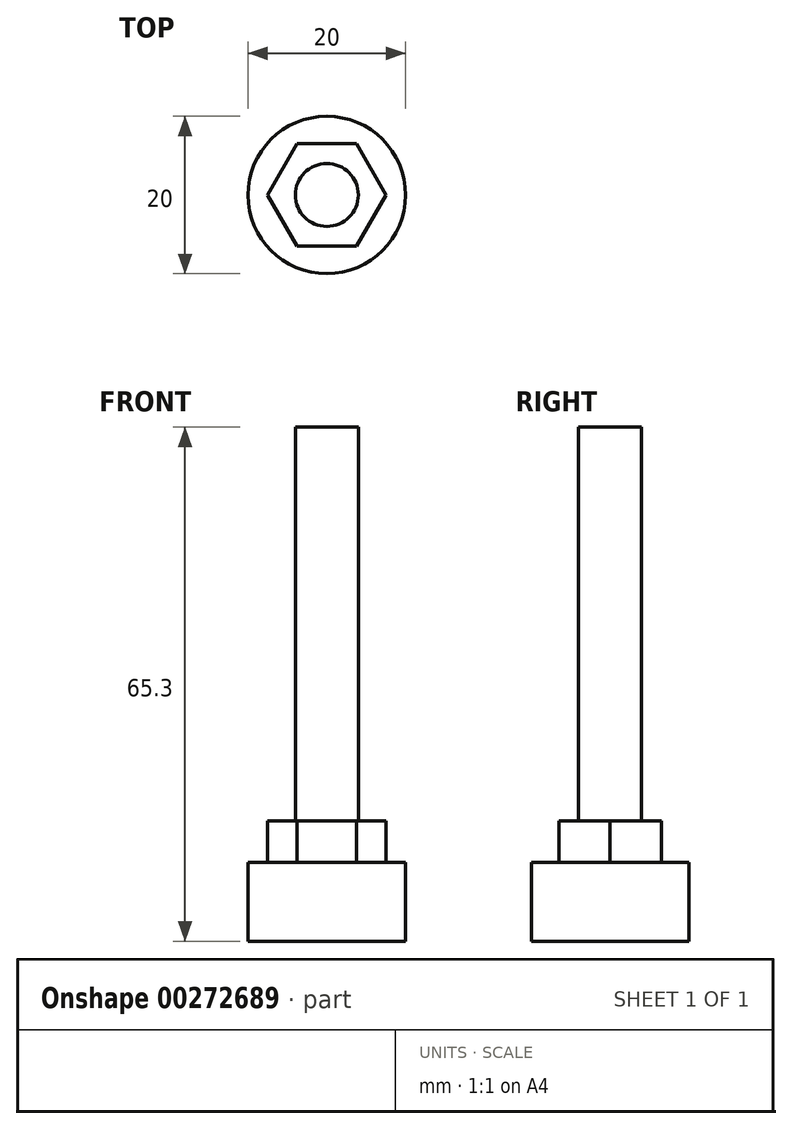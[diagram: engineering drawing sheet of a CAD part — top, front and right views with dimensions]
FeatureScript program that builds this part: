
annotation { "Feature Type Name" : "Feature", "Feature Type Description" : "" }
export const myFeature = defineFeature(function(context is Context, id is Id, definition is map)
    precondition{}
    {
        {
            var Q0;
            Q0=qCreatedBy(makeId("Right.planeOp"),FACE);
            var sketch = newSketch(context, id + "F0", { "sketchPlane" : qUnion([Q0])});
            skLineSegment(sketch, "E0", {"start": v(0, 0) * mm, "end": v(-10, 0) * mm});
            skLineSegment(sketch, "E1", {"start": v(-10, 0) * mm, "end": v(-10, 10) * mm});
            skLineSegment(sketch, "E2", {"start": v(-10, 10) * mm, "end": v(-6.5, 10) * mm});
            skLineSegment(sketch, "E3", {"start": v(-6.5, 10) * mm, "end": v(-6.5, 15.3) * mm});
            skLineSegment(sketch, "E4", {"start": v(-6.5, 15.3) * mm, "end": v(-4, 15.3) * mm});
            skLineSegment(sketch, "E5", {"start": v(-4, 15.3) * mm, "end": v(-4, 65.3) * mm});
            skLineSegment(sketch, "E6", {"start": v(-4, 65.3) * mm, "end": v(0, 65.3) * mm});
            skLineSegment(sketch, "E7", {"start": v(0, 65.3) * mm, "end": v(0, 0) * mm});
            skLineSegment(sketch, "E8", {"start": v(0, 63.9) * mm, "end": v(0, 65.3) * mm, "construction": true});
            skSolve(sketch);
        }
        {
            var Q0;
            Q0 = qSketchRegion(id + "F0", true);
            var Q1;
            Q1=sQuery(id+"F0.wireOp",EDGE,"E8");
            revolve(context, id + "F1", {"surfaceOperationType" : NewSurfaceOperationType.NEW, "entities" : qUnion([Q0]), "axis" : qUnion([Q1]), "revolveType" : RevolveType.FULL});
        }
        {
            var Q0;
            Q0=makeQuery(id+"F1.opRevolve","SWEPT_FACE",FACE,{"disambiguationData":[OSD([sQuery(id+"F0.wireOp",EDGE,"E2")])]});
            var sketch = newSketch(context, id + "F2", { "sketchPlane" : qUnion([Q0])});
            skCircle(sketch, "E9.cCircle", {"center": v(0, 0) * mm, "radius": 6.5 * mm, "construction": true});
            skLineSegment(sketch, "E9.0", {"start": v(-3.75, -6.5) * mm, "end": v(-7.5, 0) * mm});
            skLineSegment(sketch, "E9.1", {"start": v(-7.5, 0) * mm, "end": v(-3.75, 6.5) * mm});
            skLineSegment(sketch, "E9.2", {"start": v(-3.75, 6.5) * mm, "end": v(3.75, 6.5) * mm});
            skLineSegment(sketch, "E9.3", {"start": v(3.75, 6.5) * mm, "end": v(7.5, 0) * mm});
            skLineSegment(sketch, "E9.4", {"start": v(7.5, 0) * mm, "end": v(3.75, -6.5) * mm});
            skLineSegment(sketch, "E9.5", {"start": v(3.75, -6.5) * mm, "end": v(-3.75, -6.5) * mm});
            skPoint(sketch, "E9.0.midPoint", {"position": v(-5.63, -3.25) * mm});
            skSolve(sketch);
        }
        {
            var Q0;
            Q0 = qSketchRegion(id + "F2", true);
            var Q1;
            Q1=makeQuery(id+"F1.opRevolve","SWEPT_FACE",FACE,{"disambiguationData":[OSD([sQuery(id+"F0.wireOp",EDGE,"E4")])]});
            extrude(context, id + "F3", {"entities" : qUnion([Q0]), "operationType" : NewBodyOperationType.ADD, "endBound" : BoundingType.UP_TO_SURFACE, "depth" : 25 * mm, "endBoundEntityFace" : qUnion([Q1]), "offsetDistance" : 25 * mm});
        }
    });
